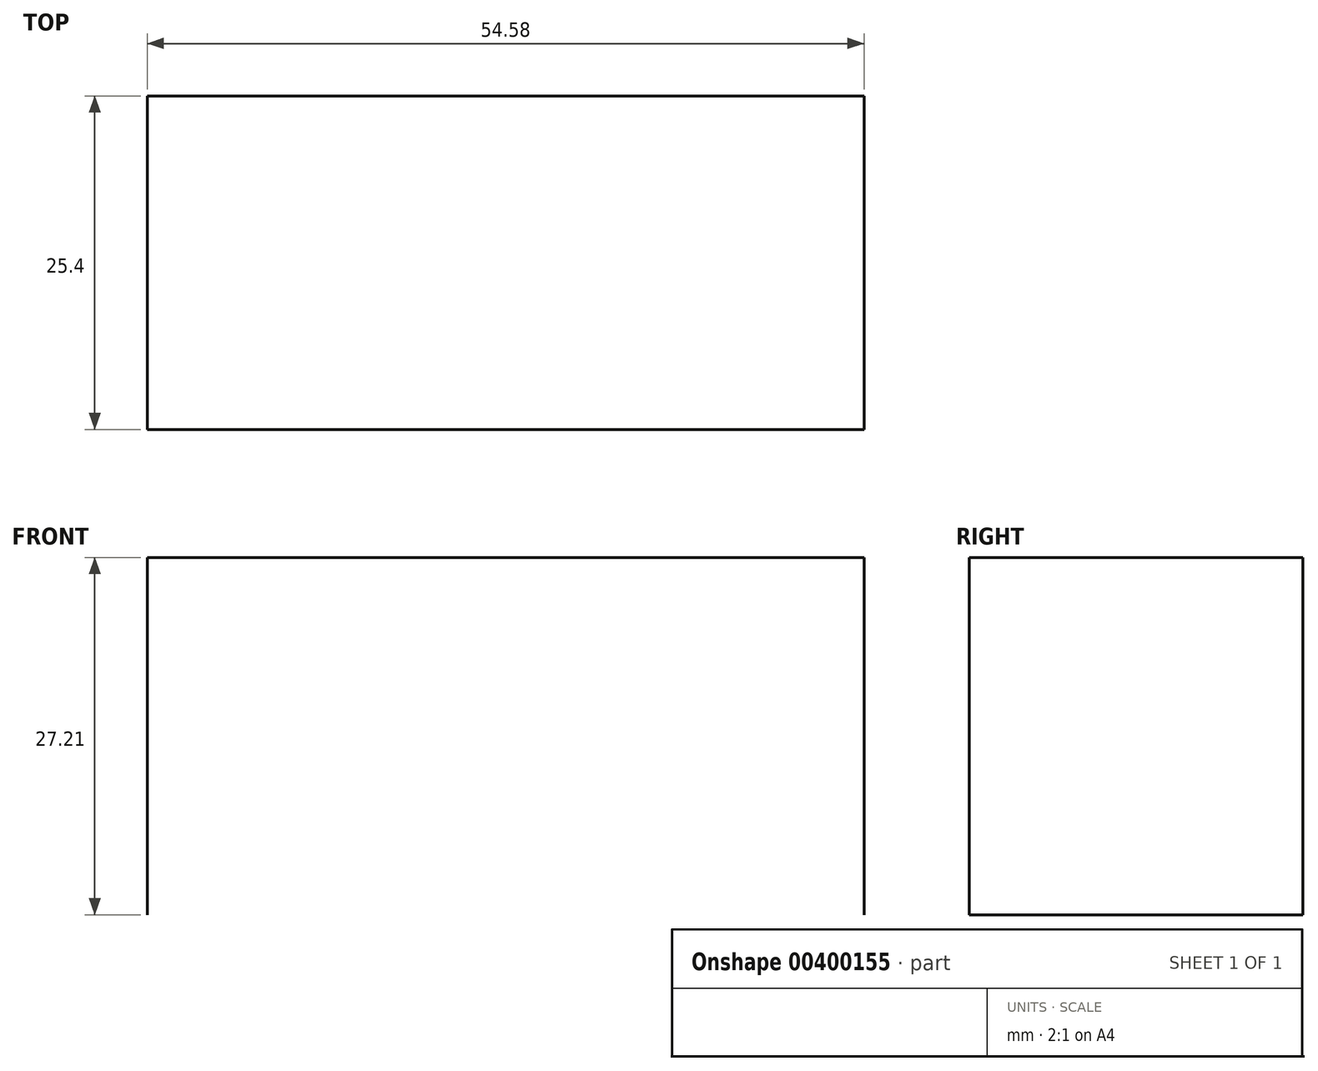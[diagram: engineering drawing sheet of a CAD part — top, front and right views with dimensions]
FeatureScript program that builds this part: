
annotation { "Feature Type Name" : "Feature", "Feature Type Description" : "" }
export const myFeature = defineFeature(function(context is Context, id is Id, definition is map)
    precondition{}
    {
        {
            var Q0;
            Q0=qCreatedBy(makeId("Front.planeOp"),FACE);
            var sketch = newSketch(context, id + "F0", { "sketchPlane" : qUnion([Q0])});
            skLineSegment(sketch, "E0.bottom", {"start": v(-28.02, 39.52) * mm, "end": v(26.56, 39.52) * mm});
            skLineSegment(sketch, "E0.top", {"start": v(-28.02, 12.3) * mm, "end": v(26.56, 12.3) * mm});
            skLineSegment(sketch, "E0.left", {"start": v(-28.02, 39.52) * mm, "end": v(-28.02, 12.3) * mm});
            skLineSegment(sketch, "E0.right", {"start": v(26.56, 39.52) * mm, "end": v(26.56, 12.3) * mm});
            skSolve(sketch);
        }
        {
            var Q0;
            Q0 = qSketchRegion(id + "F0", true);
            var Q1;
            Q1=sQuery(id+"F0.wireOp",EDGE,"E0.left");
            var Q2;
            Q2=sQuery(id+"F0.wireOp",EDGE,"E0.bottom");
            var Q3;
            Q3=sQuery(id+"F0.wireOp",EDGE,"E0.right");
            extrude(context, id + "F1", {"entities" : qUnion([Q0]), "bodyType" : ToolBodyType.SURFACE, "surfaceEntities" : qUnion([Q1, Q2, Q3]), "depth" : 25.4 * mm});
        }
    });
